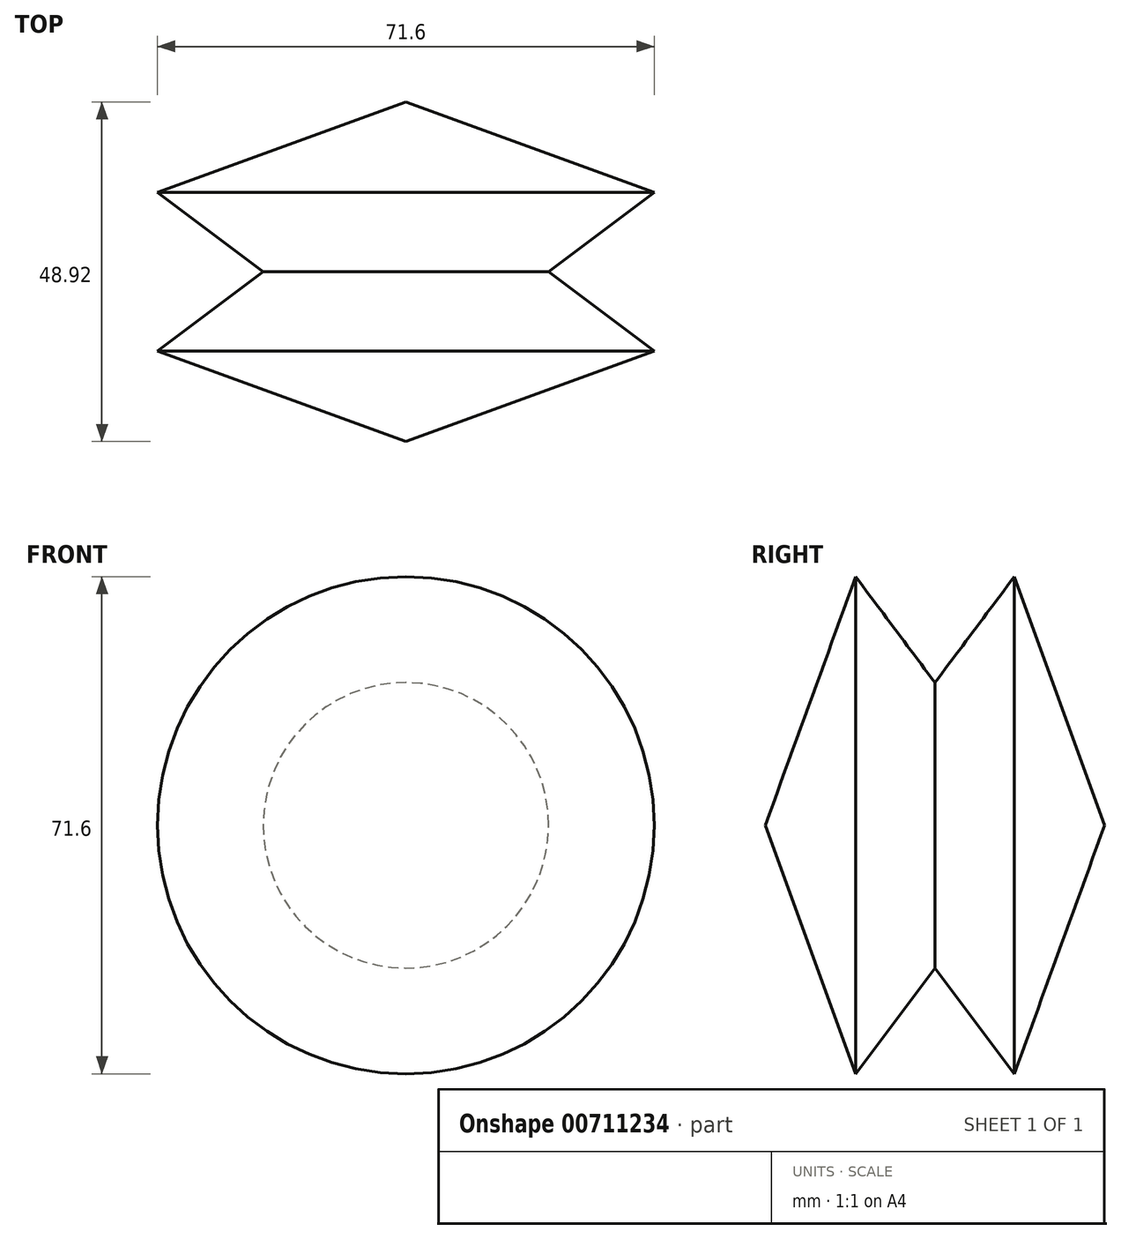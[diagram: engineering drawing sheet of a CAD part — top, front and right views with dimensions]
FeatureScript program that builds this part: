
annotation { "Feature Type Name" : "Feature", "Feature Type Description" : "" }
export const myFeature = defineFeature(function(context is Context, id is Id, definition is map)
    precondition{}
    {
        {
            var Q0;
            Q0=qCreatedBy(makeId("Top.planeOp"),FACE);
            var sketch = newSketch(context, id + "F0", { "sketchPlane" : qUnion([Q0])});
            skLineSegment(sketch, "E0", {"start": v(0, 24.46) * mm, "end": v(0, -24.46) * mm});
            skLineSegment(sketch, "E1", {"start": v(0, 24.46) * mm, "end": v(-35.8, 11.43) * mm});
            skLineSegment(sketch, "E2", {"start": v(-35.8, 11.43) * mm, "end": v(-20.56, 0) * mm});
            skLineSegment(sketch, "E3", {"start": v(-20.56, 0) * mm, "end": v(-35.8, -11.43) * mm});
            skLineSegment(sketch, "E4", {"start": v(-35.8, -11.43) * mm, "end": v(0, -24.46) * mm});
            skSolve(sketch);
        }
        {
            var Q0;
            Q0=makeQuery(id+"F0.imprint","IMPRINT",FACE,{"disambiguationData":[TD([[makeQuery(id+"F0.imprint","IMPRINT",EDGE,{"derivedFrom":sQuery(id+"F0.wireOp",EDGE,"E0")}),-1.0]])]});
            var Q1;
            Q1=sQuery(id+"F0.wireOp",EDGE,"E0");
            revolve(context, id + "F1", {"surfaceOperationType" : NewSurfaceOperationType.NEW, "entities" : qUnion([Q0]), "axis" : qUnion([Q1]), "revolveType" : RevolveType.FULL});
        }
    });
